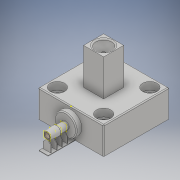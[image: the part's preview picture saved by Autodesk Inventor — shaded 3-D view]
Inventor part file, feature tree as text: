
AUTODESK INVENTOR PART (.ipt)
format: ipt  version: 2019 (Build 230136000, 136)  size: 386,560 bytes
history: native  units: mm
features: sketch x14, extrude x8, plane x7, projected_geometry x4, revolve x2, fillet x2, sweep x1, hole x1
ambient origin geometry x8: Origin, YZ Plane, XZ Plane, XY Plane, X Axis, Y Axis, Z Axis, Center Point
bodies: Solid1 (feature_tree)
feature tree (39):
  revolve  "Revolution1"  [1 undecoded]
  plane  "Work Plane1"
  extrude  "Extrusion1"  Depth=0.35mm
  plane  "Work Plane7"
  extrude  "Extrusion6"  Depth=0.75mm
  extrude  "Extrusion7"  TaperAngle=90.0deg  [1 undecoded]
  sketch  "Sketch17"  dims[d11=0.0mm d14=2.0mm d15=0.0mm d45=0.0mm]
  plane  "Work Plane8"
  sweep  "Sweep3"
  fillet  "Fillet1"  [1 undecoded]
  hole  "Hole3"  [1 undecoded]
  revolve  "Revolution2"  [1 undecoded]
  fillet  "Fillet2"  Radius=32.7mm
  plane  "Work Plane10"
  plane  "Work Plane11"
  plane  "Work Plane12"
  plane  "Work Plane13"
  extrude  "Extrusion8"  Depth=3.0mm
  extrude  "Extrusion9"  Depth=25.4mm
  extrude  "Extrusion10"  Depth=3.0mm
  extrude  "Extrusion11"  Depth=5.0mm
  extrude  "Extrusion12"  Depth=0.25mm
  sketch  "Sketch27"  dims[d85=5.08mm d86=1.15mm d87=0.25mm d88=0.25mm d89=90.0deg d90=0.5mm d92=0.0mm d93=-3.0mm d94=-6.0mm d95=-9.0mm d97=2.0mm d98=2.0mm d99=2.0mm d100=2.0mm d101=0.3mm d102=0.3mm d103=0.0mm d104=2.0mm d105=2.0mm d106=2.0mm d107=2.0mm d108=0.3mm d109=0.3mm d110=0.0mm d111=2.0mm d112=2.0mm d113=2.0mm d114=2.0mm d115=0.3mm d116=0.3mm d117=0.0mm d118=0.3mm d119=0.0mm d120=5.0mm d121=0.3mm d122=15.0mm d123=0.0mm d124=0.0mm]
  sketch  "Sketch1"  dims[d0=5.5mm d1=20.0mm]
  sketch  "Sketch2"  dims[d5=9.0mm d6=0.35mm]
  sketch  "Sketch11"  dims[d7=0.75mm d8=0.75mm]
  sketch  "Sketch16"  dims[d9=0.75mm d10=90.0deg]
  projected_geometry  "Projected Loop9"
  sketch  "Sketch18"  dims[d47=15.0mm d48=0.0mm d60=36.0mm]
  sketch  "Sketch19"  dims[d61=36.0mm d64=8.45mm d65=32.7mm d66=0.0mm]
  sketch  "Sketch21"  dims[d67=0.0mm d68=0.0mm d69=3.0mm]
  sketch  "Sketch22"  dims[d70=25.4mm d71=25.4mm]
  sketch  "Sketch23"  dims[d72=4.496mm d73=6.0mm d74=7.938mm d75=4.166mm d76=90.0deg d77=19.05mm d78=20.594885mm d79=3.0mm]
  projected_geometry  "Projected Loop10"
  sketch  "Sketch24"  dims[d80=6.0mm d81=5.0mm]
  projected_geometry  "Projected Loop11"
  sketch  "Sketch25"  dims[d82=1.8796mm d83=0.25mm]
  projected_geometry  "Projected Loop12"
  sketch  "Sketch26"  dims[d84=2.413mm]
note: 5 required parameter values undecoded (feature->parameter linkage not recoverable at this tier; creation-order binding heuristic only, values carry confidence <= 0.55)